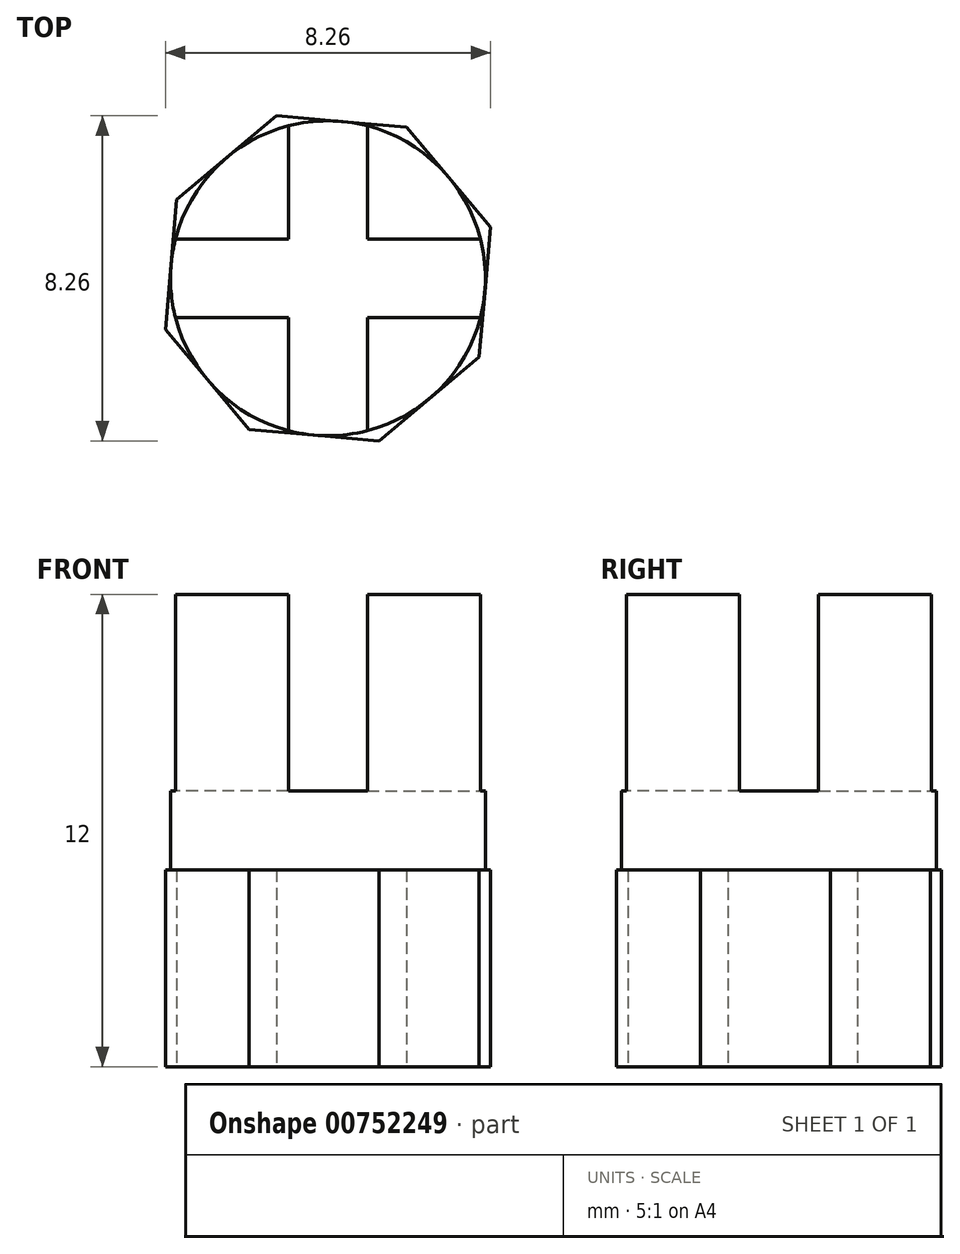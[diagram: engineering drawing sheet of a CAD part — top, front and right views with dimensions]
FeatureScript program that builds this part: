
annotation { "Feature Type Name" : "Feature", "Feature Type Description" : "" }
export const myFeature = defineFeature(function(context is Context, id is Id, definition is map)
    precondition{}
    {
        {
            var Q0;
            Q0=qCreatedBy(makeId("Top.planeOp"),FACE);
            var sketch = newSketch(context, id + "F0", { "sketchPlane" : qUnion([Q0])});
            skCircle(sketch, "E0.cCircle", {"center": v(0, 0) * mm, "radius": 4 * mm, "construction": true});
            skLineSegment(sketch, "E0.0", {"start": v(-2, -3.84) * mm, "end": v(-4.13, -1.3) * mm});
            skLineSegment(sketch, "E0.1", {"start": v(-4.13, -1.3) * mm, "end": v(-3.84, 2) * mm});
            skLineSegment(sketch, "E0.2", {"start": v(-3.84, 2) * mm, "end": v(-1.3, 4.13) * mm});
            skLineSegment(sketch, "E0.3", {"start": v(-1.3, 4.13) * mm, "end": v(2, 3.84) * mm});
            skLineSegment(sketch, "E0.4", {"start": v(2, 3.84) * mm, "end": v(4.13, 1.3) * mm});
            skLineSegment(sketch, "E0.5", {"start": v(4.13, 1.3) * mm, "end": v(3.84, -2) * mm});
            skLineSegment(sketch, "E0.6", {"start": v(3.84, -2) * mm, "end": v(1.3, -4.13) * mm});
            skLineSegment(sketch, "E0.7", {"start": v(1.3, -4.13) * mm, "end": v(-2, -3.84) * mm});
            skPoint(sketch, "E0.0.midPoint", {"position": v(-3.06, -2.57) * mm});
            skSolve(sketch);
        }
        {
            var Q0;
            Q0 = qSketchRegion(id + "F0", true);
            extrude(context, id + "F1", {"entities" : qUnion([Q0]), "depth" : 5 * mm, "offsetDistance" : 25 * mm});
        }
        {
            var Q0;
            Q0=makeQuery(id+"F1.opExtrude","CAP_FACE",FACE,{"disambiguationData":[OSD([sQuery(id+"F0.wireOp",EDGE,"E0.0"),sQuery(id+"F0.wireOp",EDGE,"E0.1"),sQuery(id+"F0.wireOp",EDGE,"E0.2"),sQuery(id+"F0.wireOp",EDGE,"E0.3"),sQuery(id+"F0.wireOp",EDGE,"E0.4"),sQuery(id+"F0.wireOp",EDGE,"E0.5"),sQuery(id+"F0.wireOp",EDGE,"E0.6"),sQuery(id+"F0.wireOp",EDGE,"E0.7")])],"isStart":false});
            var sketch = newSketch(context, id + "F2", { "sketchPlane" : qUnion([Q0])});
            skCircle(sketch, "E1", {"center": v(0, 0) * mm, "radius": 4 * mm});
            skSolve(sketch);
        }
        {
            var Q0;
            Q0 = qSketchRegion(id + "F2", true);
            extrude(context, id + "F3", {"entities" : qUnion([Q0]), "operationType" : NewBodyOperationType.ADD, "depth" : 2 * mm, "offsetDistance" : 25 * mm});
        }
        {
            var Q0;
            Q0=makeQuery(id+"F3.opExtrude","CAP_FACE",FACE,{"disambiguationData":[OSD([sQuery(id+"F2.wireOp",EDGE,"E1")])],"isStart":false});
            var sketch = newSketch(context, id + "F4", { "sketchPlane" : qUnion([Q0])});
            skSolve(sketch);
        }
        {
            var Q0;
            Q0=makeQuery(id+"F4.imprint","IMPRINT",FACE,{"disambiguationData":[TD([[makeQuery(id+"F4.imprint","IMPRINT",EDGE,{"derivedFrom":makeQuery(id+"F3.opExtrude","CAP_EDGE",EDGE,{"disambiguationData":[OSD([sQuery(id+"F2.wireOp",EDGE,"E1")])],"isStart":false})}),1.0]])]});
            var sketch = newSketch(context, id + "F5", { "sketchPlane" : qUnion([Q0])});
            skLineSegment(sketch, "E2.bottom", {"start": v(1, 1) * mm, "end": v(-1, 1) * mm, "construction": true});
            skLineSegment(sketch, "E2.top", {"start": v(1, -1) * mm, "end": v(-1, -1) * mm, "construction": true});
            skLineSegment(sketch, "E2.left", {"start": v(1, 1) * mm, "end": v(1, -1) * mm, "construction": true});
            skLineSegment(sketch, "E2.right", {"start": v(-1, 1) * mm, "end": v(-1, -1) * mm, "construction": true});
            skPoint(sketch, "E2.middle", {"position": v(0, 0) * mm});
            skLineSegment(sketch, "E3", {"start": v(-1, -1) * mm, "end": v(-1, -3.87) * mm});
            skLineSegment(sketch, "E4", {"start": v(-1, -1) * mm, "end": v(-3.87, -1) * mm});
            skLineSegment(sketch, "E5", {"start": v(-1, 1) * mm, "end": v(-3.87, 1) * mm});
            skLineSegment(sketch, "E6", {"start": v(-1, 1) * mm, "end": v(-1, 3.87) * mm});
            skLineSegment(sketch, "E7", {"start": v(1, 1) * mm, "end": v(1, 3.87) * mm});
            skLineSegment(sketch, "E8", {"start": v(1, 1) * mm, "end": v(3.87, 1) * mm});
            skLineSegment(sketch, "E9", {"start": v(1, -1) * mm, "end": v(3.87, -1) * mm});
            skLineSegment(sketch, "E10", {"start": v(1, -1) * mm, "end": v(1, -3.87) * mm});
            skSolve(sketch);
        }
        {
            var Q0;
            {var subQ0=sQuery(id+"F5.wireOp",EDGE,"E5");Q0=makeQuery(id+"F5.imprint","IMPRINT",FACE,{"disambiguationData":[TD([[makeQuery(id+"F5.imprint","IMPRINT",EDGE,{"derivedFrom":subQ0}),-1.0]])]});}
            var Q1;
            {var subQ0=sQuery(id+"F5.wireOp",EDGE,"E7");Q1=makeQuery(id+"F5.imprint","IMPRINT",FACE,{"disambiguationData":[TD([[makeQuery(id+"F5.imprint","IMPRINT",EDGE,{"derivedFrom":subQ0}),-1.0]])]});}
            var Q2;
            {var subQ0=sQuery(id+"F5.wireOp",EDGE,"E9");Q2=makeQuery(id+"F5.imprint","IMPRINT",FACE,{"disambiguationData":[TD([[makeQuery(id+"F5.imprint","IMPRINT",EDGE,{"derivedFrom":subQ0}),-1.0]])]});}
            var Q3;
            {var subQ0=sQuery(id+"F5.wireOp",EDGE,"E3");Q3=makeQuery(id+"F5.imprint","IMPRINT",FACE,{"disambiguationData":[TD([[makeQuery(id+"F5.imprint","IMPRINT",EDGE,{"derivedFrom":subQ0}),-1.0]])]});}
            extrude(context, id + "F6", {"entities" : qUnion([Q0, Q1, Q2, Q3]), "operationType" : NewBodyOperationType.ADD, "depth" : 5 * mm, "offsetDistance" : 25 * mm});
        }
    });
